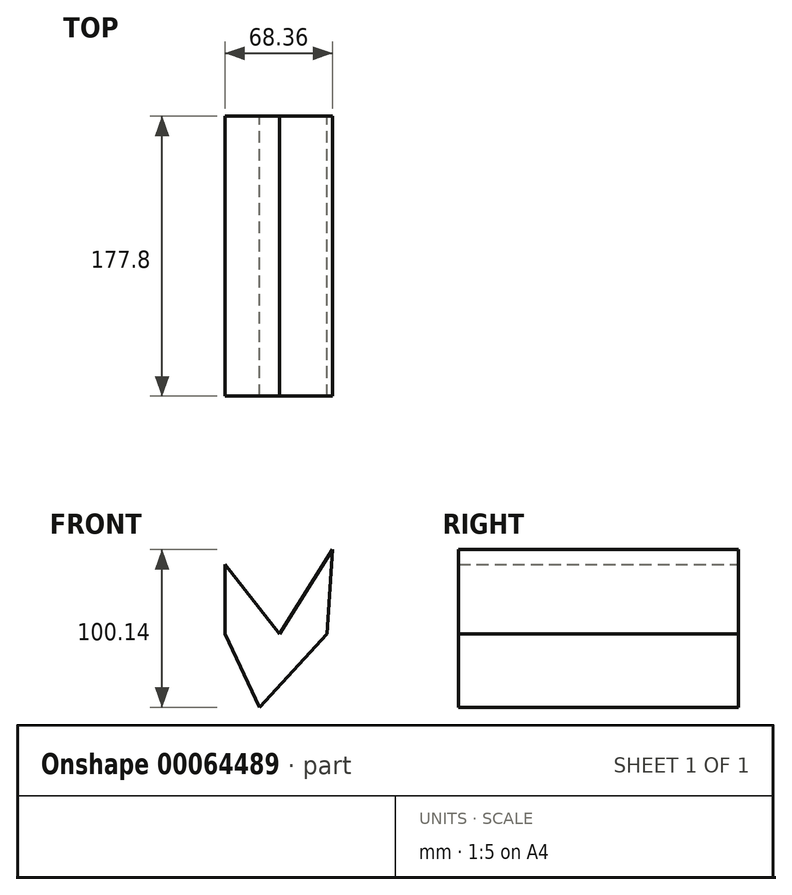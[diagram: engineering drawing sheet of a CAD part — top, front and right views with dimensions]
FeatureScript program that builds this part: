
annotation { "Feature Type Name" : "Feature", "Feature Type Description" : "" }
export const myFeature = defineFeature(function(context is Context, id is Id, definition is map)
    precondition{}
    {
        {
            var Q0;
            Q0=qCreatedBy(makeId("Front.planeOp"),FACE);
            var sketch = newSketch(context, id + "F0", { "sketchPlane" : qUnion([Q0])});
            skLineSegment(sketch, "E0", {"start": v(-60.2, 44.1) * mm, "end": v(-60.2, 0) * mm});
            skLineSegment(sketch, "E1", {"start": v(-60.2, 0) * mm, "end": v(-38.27, -46.5) * mm});
            skLineSegment(sketch, "E2", {"start": v(-38.27, -46.5) * mm, "end": v(4.6, 0) * mm});
            skLineSegment(sketch, "E3", {"start": v(4.6, 0) * mm, "end": v(8.16, 53.63) * mm});
            skLineSegment(sketch, "E4", {"start": v(8.16, 53.63) * mm, "end": v(-25.51, 0) * mm});
            skLineSegment(sketch, "E5", {"start": v(-25.51, 0) * mm, "end": v(-60.2, 44.1) * mm});
            skSolve(sketch);
        }
        {
            var Q0;
            Q0=makeQuery(id+"F0.imprint","IMPRINT",FACE,{"disambiguationData":[TD([[makeQuery(id+"F0.imprint","IMPRINT",EDGE,{"derivedFrom":sQuery(id+"F0.wireOp",EDGE,"E0")}),1.0]])]});
            extrude(context, id + "F1", {"entities" : qUnion([Q0]), "depth" : 177.8 * mm});
        }
    });
